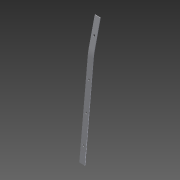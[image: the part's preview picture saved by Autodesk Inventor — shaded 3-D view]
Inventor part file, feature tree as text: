
AUTODESK INVENTOR PART (.ipt)
format: ipt  version: 2015 (Build 190159000, 159)  size: 134,144 bytes
history: native  units: mm
features: reference x11, sketch x6, other x3, hole x3, sweep x1
ambient origin geometry x8: Origin, YZ Plane, XZ Plane, XY Plane, X Axis, Y Axis, Z Axis, Center Point
bodies: Body1 (feature_tree)
feature tree (24):
  other  "Listwa_siedziska_lewa"
  sweep  "Przeciągnięcie1"
  hole  "Otwór1"  [1 undecoded]
  other  "Gięcie części1"
  hole  "Otwór3"  [1 undecoded]
  hole  "Otwór4"  [1 undecoded]
  sketch  "Szkic1"
  sketch  "Szkic2"
  sketch  "Szkic4"
  reference  "Odniesienie1"
  reference  "Odniesienie2"
  reference  "Odniesienie3"
  reference  "Odniesienie4"
  sketch  "Szkic5"
  sketch  "Szkic6"
  other  "Bryła2"
  reference  "Odniesienie6"
  reference  "Odniesienie7"
  reference  "Odniesienie8"
  reference  "Odniesienie9"
  reference  "Odniesienie10"
  reference  "Odniesienie11"
  sketch  "Szkic7"
  reference  "Odniesienie12"
note: 3 required parameter values undecoded (feature->parameter linkage not recoverable at this tier; creation-order binding heuristic only, values carry confidence <= 0.55)
